# Revit family: Faucet-Kitchen-KALLISTA-VIR_STIL_MINIMAL-P25517
name_source: partatom
category: Plumbing Fixtures
units: mm (PartAtom-declared; Revit-internal decimal feet)

## family parameters
Cut with Voids When Loaded = No
Host = Face
Maintain Annotation Orientation = No
OmniClass Number = 23.31.11.00
OmniClass Title = Faucets
Part Type = Normal
Room Calculation Point = No
Round Connector Dimension = Use Diameter
Shared = No

## types (4) — shared parameters
ADA Compliant = Yes
Assembly Code = D2010
CW Connection = Yes
Cold Water Inlet = Cold Water Inlet
Date Modified = 03/09/2022
Default Elevation = 36"
Description = PULL-DOWN KITCHEN FAUCET
Drain Included = No
Flow Rate = 2 GPM
HW Connection = Yes
Handle Clearance = 3 5/16"
Height = 16 15/16"
Hot Water Inlet = Hot Water Inlet
Length = 9 9/16"
Manufacturer = Kallista Co.
Master Format 2014 = 22 41 39
Master Format 2014 Name = Residential Faucets, Supplies, and Trim
Material = Premium Metal Construction
Pressure = 60.00 psi
Product Documentation Link = https://resources.kohler.com
Product Name = VIR STIL MINIMAL
Product Page URL = https://www.kallista.com
Spout Reach = 9 9/16"
URL = http://www.kallista.com
Vent Connection = No
Waste Connection = No
Waste Water Outlet = Waste Water Outlet
WaterSense Certified = No
Width = 2 3/4"

## per-type parameters (varying)
| type | Finish | Model | Type |
| CP-Chrome | Kallista-Metal-CP-Chrome | P25517-00-CP | 1 |
| VS-Stainless | Kallista-Metal-VS-Stainless | P25517-00-VS | 2 |
| SN-Polished Nickel | Kallista-Metal-SN-Polished_Nickel | P25517-00-SN | 3 |
| BN-Brushed Nickel | Kallista-Metal-BN-Brushed_Nickel | P25517-00-BN | 4 |

## geometry (parser evidence)
native form markers: Sweep x5
no freeform markers — native parametric forms only
